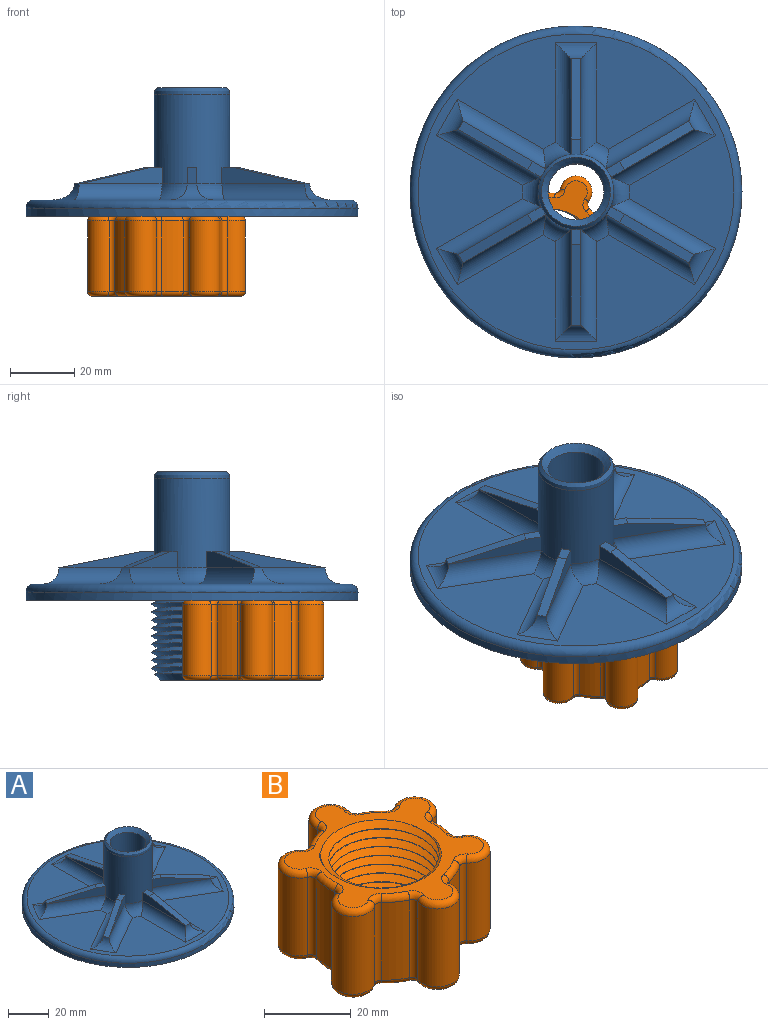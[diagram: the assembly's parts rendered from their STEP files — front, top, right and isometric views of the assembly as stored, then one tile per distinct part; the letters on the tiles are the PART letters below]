
ASSEMBLY  parts=2 mates=1
PART A: 63 faces, bbox 112x112x65.9 mm
  f0: plane 98.5x98.5mm, normal (0,0,1), area 4384.6mm2, adj f38,f39,f40,f41,f42,f43,f44,f45
  f1: cylinder r=8.75mm len=63mm, axis (0,0,-1), area 3463.6mm2, adj f5,f36
  f2: plane 103.5x103.5mm, normal (0,0,-1), area 7902.7mm2, adj f3,f8
  f3: cylinder r=51.75mm len=103.5mm, axis (0,0,-1), area 812.9mm2, adj f2,f38
  f4: cylinder r=11.75mm len=27.76mm, axis (0,0,-1), area 1959.5mm2, adj f13,f14,f15,f17,f18,f19,f21,f22
  f5: plane 19.5x19.5mm, normal (0,0,-1), area 58.1mm2, adj f1,f6
  f6: cone r=9.75mm half-angle=45deg, axis (0,0,1), area 180.7mm2, adj f5,f9,f11
  f7: plane 2.52x1.91mm, normal (0.5,-0.87,0), area 2.8mm2, adj f8,f9,f10,f11
  f8: cylinder r=12.75mm len=25.5mm, axis (0,0,1), area 166.9mm2, adj f2,f7,f10
  f9: bspline ~29.37x27.92mm, area 1889.3mm2, adj f6,f7,f10,f11
  f10: bspline ~25.47x25.46mm, area 3.2mm2, adj f7,f8,f9
  f11: bspline ~29.37x27.92mm, area 1795.1mm2, adj f6,f7,f9
  f12: plane 23.15x15.1mm, normal (-0.17,-0.1,0.98), area 76.5mm2, adj f13,f14,f15,f42
  f13: plane 5.7x5.02mm, normal (0,0,1), area 14.3mm2, adj f4,f12,f14,f15
  f14: plane 25.85x14.92mm, normal (-0.5,0.87,0), area 86.7mm2, adj f4,f12,f13,f44
  f15: plane 25.85x14.92mm, normal (0.5,-0.87,0), area 86.7mm2, adj f4,f12,f13,f40
  f16: plane 25x5mm, normal (0,-0.2,0.98), area 76.5mm2, adj f17,f18,f19,f43
  f17: plane 4.85x3mm, normal (0,0,1), area 14.3mm2, adj f4,f16,f18,f19
  f18: plane 29.85x5mm, normal (-1,0,0), area 86.7mm2, adj f4,f16,f17,f41
  f19: plane 29.85x5mm, normal (1,0,0), area 86.7mm2, adj f4,f16,f17,f45
  f20: plane 23.15x15.1mm, normal (-0.17,0.1,0.98), area 76.5mm2, adj f21,f22,f23,f50
  f21: plane 5.7x5.02mm, normal (0,0,1), area 14.3mm2, adj f4,f20,f22,f23
  f22: plane 25.85x14.92mm, normal (0.5,0.87,0), area 86.7mm2, adj f4,f20,f21,f52
  f23: plane 25.85x14.92mm, normal (-0.5,-0.87,0), area 86.7mm2, adj f4,f20,f21,f48
  f24: plane 23.15x15.1mm, normal (0.17,-0.1,0.98), area 76.5mm2, adj f25,f26,f27,f51
  f25: plane 5.7x5.02mm, normal (0,0,1), area 14.3mm2, adj f4,f24,f26,f27
  f26: plane 25.85x14.92mm, normal (-0.5,-0.87,0), area 86.7mm2, adj f4,f24,f25,f49
  f27: plane 25.85x14.92mm, normal (0.5,0.87,0), area 86.7mm2, adj f4,f24,f25,f53
  f28: plane 23.15x15.1mm, normal (0.17,0.1,0.98), area 76.5mm2, adj f29,f30,f31,f59
  f29: plane 5.7x5.02mm, normal (0,0,1), area 14.3mm2, adj f4,f28,f30,f31
  f30: plane 25.85x14.92mm, normal (0.5,-0.87,0), area 86.7mm2, adj f4,f28,f29,f57
  f31: plane 25.85x14.92mm, normal (-0.5,0.87,0), area 86.7mm2, adj f4,f28,f29,f61
  f32: plane 25x5mm, normal (0,0.2,0.98), area 76.5mm2, adj f33,f34,f35,f58
  f33: plane 4.85x3mm, normal (0,0,1), area 14.3mm2, adj f4,f32,f34,f35
  f34: plane 29.85x5mm, normal (1,0,0), area 86.7mm2, adj f4,f32,f33,f60
  f35: plane 29.85x5mm, normal (-1,0,0), area 86.7mm2, adj f4,f32,f33,f56
  f36: cone r=10.75mm half-angle=45deg, axis (0,0,1), area 173.3mm2, adj f1,f37
  f37: bspline ~23.5x23.5mm, area 188.6mm2, adj f4,f36
  f38: torus R=49.25mm, axis (0,0,1), area 1254.5mm2, adj f0,f3
  f39: torus R=16.75mm, axis (0,0,1), area 53.6mm2, adj f0,f4,f40,f41
  f40: cylinder r=5mm len=32.68mm, axis (-0.87,-0.5,0), area 239.2mm2, adj f0,f15,f39,f42
  f41: cylinder r=5mm len=34.85mm, axis (0,1,0), area 239.2mm2, adj f0,f18,f39,f43
  f42: cylinder r=5mm len=13.76mm, axis (0.5,-0.87,0), area 62.8mm2, adj f0,f12,f40,f44
  f43: cylinder r=5mm len=13mm, axis (1,0,0), area 62.8mm2, adj f0,f16,f41,f45
  f44: cylinder r=5mm len=32.68mm, axis (0.87,0.5,0), area 239.2mm2, adj f0,f14,f42,f46
  f45: cylinder r=5mm len=34.85mm, axis (0,-1,0), area 239.2mm2, adj f0,f19,f43,f47
  f46: torus R=16.75mm, axis (0,0,1), area 53.6mm2, adj f0,f4,f44,f48
  f47: torus R=16.75mm, axis (0,0,1), area 53.6mm2, adj f0,f4,f45,f49
  f48: cylinder r=5mm len=32.68mm, axis (-0.87,0.5,0), area 239.2mm2, adj f0,f23,f46,f50
  f49: cylinder r=5mm len=32.68mm, axis (-0.87,0.5,0), area 239.2mm2, adj f0,f26,f47,f51
  f50: cylinder r=5mm len=13.76mm, axis (-0.5,-0.87,0), area 62.8mm2, adj f0,f20,f48,f52
  f51: cylinder r=5mm len=13.76mm, axis (0.5,0.87,0), area 62.8mm2, adj f0,f24,f49,f53
  f52: cylinder r=5mm len=32.68mm, axis (0.87,-0.5,0), area 239.2mm2, adj f0,f22,f50,f54
  f53: cylinder r=5mm len=32.68mm, axis (0.87,-0.5,0), area 239.2mm2, adj f0,f27,f51,f55
  f54: torus R=16.75mm, axis (0,0,1), area 53.6mm2, adj f0,f4,f52,f56
  f55: torus R=16.75mm, axis (0,0,1), area 53.6mm2, adj f0,f4,f53,f57
  f56: cylinder r=5mm len=34.85mm, axis (0,1,0), area 239.2mm2, adj f0,f35,f54,f58
  f57: cylinder r=5mm len=32.68mm, axis (-0.87,-0.5,0), area 239.2mm2, adj f0,f30,f55,f59
  f58: cylinder r=5mm len=13mm, axis (-1,0,0), area 62.8mm2, adj f0,f32,f56,f60
  f59: cylinder r=5mm len=13.76mm, axis (-0.5,0.87,0), area 62.8mm2, adj f0,f28,f57,f61
  f60: cylinder r=5mm len=34.85mm, axis (0,-1,0), area 239.2mm2, adj f0,f34,f58,f62
  f61: cylinder r=5mm len=32.68mm, axis (0.87,0.5,0), area 239.2mm2, adj f0,f31,f59,f62
  f62: torus R=16.75mm, axis (0,0,1), area 53.6mm2, adj f0,f4,f60,f61
PART B: 77 faces, bbox 48.4x51.5x29.5 mm
  f0: plane 47.69x44.57mm, normal (0,0,1), area 501.2mm2, adj f13,f15,f16,f17,f18,f19,f21,f22
  f1: plane 47.69x44.57mm, normal (0,0,-1), area 501.2mm2, adj f13,f15,f16,f24,f25,f28,f29,f34
  f2: cylinder r=5mm len=22mm, axis (0,0,1), area 398.3mm2, adj f62,f71,f72,f76
  f3: cylinder r=17.75mm len=22mm, axis (0,0,-1), area 147.9mm2, adj f60,f61,f70,f71
  f4: cylinder r=5mm len=22mm, axis (0,0,1), area 398.3mm2, adj f52,f53,f64,f65
  f5: cylinder r=17.75mm len=22mm, axis (0,0,-1), area 147.9mm2, adj f63,f64,f72,f73
  f6: cylinder r=5mm len=22mm, axis (0,0,1), area 398.3mm2, adj f32,f33,f43,f44
  f7: cylinder r=17.75mm len=22mm, axis (0,0,-1), area 147.9mm2, adj f42,f43,f53,f54
  f8: cylinder r=5mm len=22mm, axis (0,0,1), area 398.3mm2, adj f17,f20,f23,f24
  f9: cylinder r=17.75mm len=22mm, axis (0,0,-1), area 147.9mm2, adj f22,f23,f33,f34
  f10: cylinder r=5mm len=22mm, axis (0,0,1), area 398.3mm2, adj f30,f31,f39,f40
  f11: cylinder r=17.75mm len=22mm, axis (0,0,-1), area 147.9mm2, adj f20,f21,f29,f30
  f12: cylinder r=5mm len=22mm, axis (0,0,1), area 398.3mm2, adj f50,f51,f59,f60
  f13: cylinder r=12.75mm len=25.5mm, axis (0,0,-1), area 227.7mm2, adj f0,f1,f15,f16
  f14: cylinder r=17.75mm len=22mm, axis (0,0,-1), area 147.9mm2, adj f40,f41,f49,f50
  f15: bspline ~34.5x29.87mm, area 2264.3mm2, adj f0,f1,f13,f16
  f16: bspline ~34.5x29.87mm, area 2090.6mm2, adj f0,f1,f13,f15
  f17: torus R=3.5mm, axis (0,0,1), area 38mm2, adj f0,f8,f18,f19
  f18: torus R=3mm, axis (0,0,1), area 7.1mm2, adj f0,f17,f20,f21
  f19: torus R=3mm, axis (0,0,1), area 7.1mm2, adj f0,f17,f22,f23
  f20: cylinder r=1.5mm len=22mm, axis (0,0,-1), area 48.7mm2, adj f8,f11,f18,f25
  f21: torus R=16.25mm, axis (0,0,1), area 15.4mm2, adj f0,f11,f18,f26
  f22: torus R=16.25mm, axis (0,0,1), area 15.4mm2, adj f0,f9,f19,f27
  f23: cylinder r=1.5mm len=22mm, axis (0,0,-1), area 48.7mm2, adj f8,f9,f19,f28
  f24: torus R=3.5mm, axis (0,0,-1), area 38mm2, adj f1,f8,f25,f28
  f25: torus R=3mm, axis (0,0,-1), area 7.1mm2, adj f1,f20,f24,f29
  f26: torus R=3mm, axis (0,0,1), area 7.1mm2, adj f0,f21,f30,f31
  f27: torus R=3mm, axis (0,0,1), area 7.1mm2, adj f0,f22,f32,f33
  f28: torus R=3mm, axis (0,0,-1), area 7.1mm2, adj f1,f23,f24,f34
  f29: torus R=16.25mm, axis (0,0,-1), area 15.4mm2, adj f1,f11,f25,f35
  f30: cylinder r=1.5mm len=22mm, axis (0,0,-1), area 48.7mm2, adj f10,f11,f26,f35
  f31: torus R=3.5mm, axis (0,0,1), area 38mm2, adj f0,f10,f26,f36
  f32: torus R=3.5mm, axis (0,0,1), area 38mm2, adj f0,f6,f27,f37
  f33: cylinder r=1.5mm len=22mm, axis (0,0,-1), area 48.7mm2, adj f6,f9,f27,f38
  f34: torus R=16.25mm, axis (0,0,-1), area 15.4mm2, adj f1,f9,f28,f38
  f35: torus R=3mm, axis (0,0,-1), area 7.1mm2, adj f1,f29,f30,f39
  f36: torus R=3mm, axis (0,0,1), area 7.1mm2, adj f0,f31,f40,f41
  f37: torus R=3mm, axis (0,0,1), area 7.1mm2, adj f0,f32,f42,f43
  f38: torus R=3mm, axis (0,0,-1), area 7.1mm2, adj f1,f33,f34,f44
  f39: torus R=3.5mm, axis (0,0,-1), area 38mm2, adj f1,f10,f35,f45
  f40: cylinder r=1.5mm len=22mm, axis (0,0,-1), area 48.7mm2, adj f10,f14,f36,f45
  f41: torus R=16.25mm, axis (0,0,1), area 15.4mm2, adj f0,f14,f36,f46
  f42: torus R=16.25mm, axis (0,0,1), area 15.4mm2, adj f0,f7,f37,f47
  f43: cylinder r=1.5mm len=22mm, axis (0,0,-1), area 48.7mm2, adj f6,f7,f37,f48
  f44: torus R=3.5mm, axis (0,0,-1), area 38mm2, adj f1,f6,f38,f48
  f45: torus R=3mm, axis (0,0,-1), area 7.1mm2, adj f1,f39,f40,f49
  f46: torus R=3mm, axis (0,0,1), area 7.1mm2, adj f0,f41,f50,f51
  f47: torus R=3mm, axis (0,0,1), area 7.1mm2, adj f0,f42,f52,f53
  f48: torus R=3mm, axis (0,0,-1), area 7.1mm2, adj f1,f43,f44,f54
  f49: torus R=16.25mm, axis (0,0,-1), area 15.4mm2, adj f1,f14,f45,f55
  f50: cylinder r=1.5mm len=22mm, axis (0,0,-1), area 48.7mm2, adj f12,f14,f46,f55
  f51: torus R=3.5mm, axis (0,0,1), area 38mm2, adj f0,f12,f46,f56
  f52: torus R=3.5mm, axis (0,0,1), area 38mm2, adj f0,f4,f47,f57
  f53: cylinder r=1.5mm len=22mm, axis (0,0,-1), area 48.7mm2, adj f4,f7,f47,f58
  f54: torus R=16.25mm, axis (0,0,-1), area 15.4mm2, adj f1,f7,f48,f58
  f55: torus R=3mm, axis (0,0,-1), area 7.1mm2, adj f1,f49,f50,f59
  f56: torus R=3mm, axis (0,0,1), area 7.1mm2, adj f0,f51,f60,f61
  f57: torus R=3mm, axis (0,0,1), area 7.1mm2, adj f0,f52,f63,f64
  f58: torus R=3mm, axis (0,0,-1), area 7.1mm2, adj f1,f53,f54,f65
  f59: torus R=3.5mm, axis (0,0,-1), area 38mm2, adj f1,f12,f55,f66
  f60: cylinder r=1.5mm len=22mm, axis (0,0,-1), area 48.7mm2, adj f3,f12,f56,f66
  f61: torus R=16.25mm, axis (0,0,1), area 15.4mm2, adj f0,f3,f56,f67
  f62: torus R=3.5mm, axis (0,0,1), area 38mm2, adj f0,f2,f67,f68
  f63: torus R=16.25mm, axis (0,0,1), area 15.4mm2, adj f0,f5,f57,f68
  f64: cylinder r=1.5mm len=22mm, axis (0,0,-1), area 48.7mm2, adj f4,f5,f57,f69
  f65: torus R=3.5mm, axis (0,0,-1), area 38mm2, adj f1,f4,f58,f69
  f66: torus R=3mm, axis (0,0,-1), area 7.1mm2, adj f1,f59,f60,f70
  f67: torus R=3mm, axis (0,0,1), area 7.1mm2, adj f0,f61,f62,f71
  f68: torus R=3mm, axis (0,0,1), area 7.1mm2, adj f0,f62,f63,f72
  f69: torus R=3mm, axis (0,0,-1), area 7.1mm2, adj f1,f64,f65,f73
  f70: torus R=16.25mm, axis (0,0,-1), area 15.4mm2, adj f1,f3,f66,f74
  f71: cylinder r=1.5mm len=22mm, axis (0,0,-1), area 48.7mm2, adj f2,f3,f67,f74
  f72: cylinder r=1.5mm len=22mm, axis (0,0,-1), area 48.7mm2, adj f2,f5,f68,f75
  f73: torus R=16.25mm, axis (0,0,-1), area 15.4mm2, adj f1,f5,f69,f75
  f74: torus R=3mm, axis (0,0,-1), area 7.1mm2, adj f1,f70,f71,f76
  f75: torus R=3mm, axis (0,0,-1), area 7.1mm2, adj f1,f72,f73,f76
  f76: torus R=3.5mm, axis (0,0,-1), area 38mm2, adj f1,f2,f74,f75
PLACE A at identity fixed
PLACE B rot(axis=(0.71,0.71,0),180deg) t=(-7.96,-18.05,0)mm
MATE fastened B.f4 <-> A.f1  axis (0,0,1) through (0,0,0)mm
